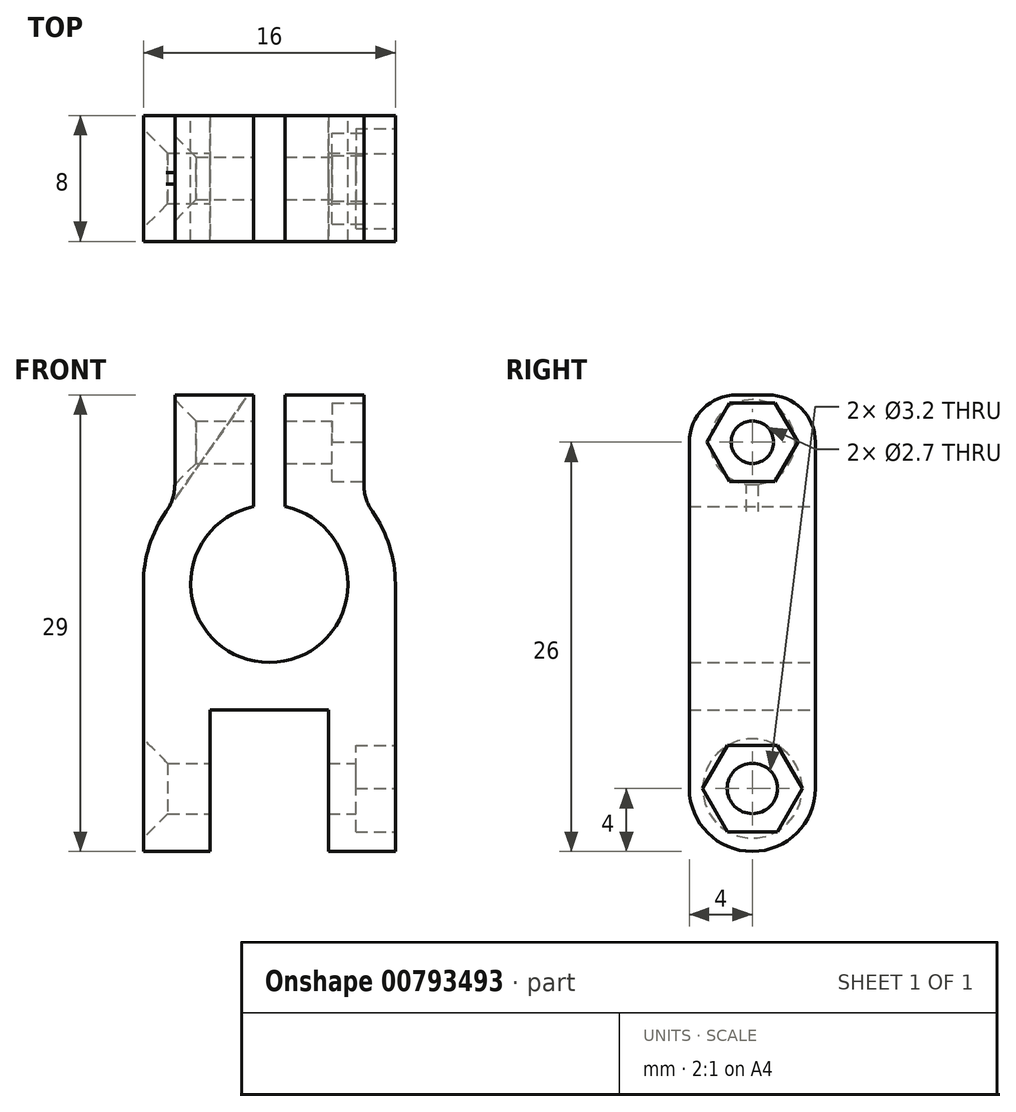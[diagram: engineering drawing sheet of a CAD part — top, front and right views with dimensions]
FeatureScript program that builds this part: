
annotation { "Feature Type Name" : "Feature", "Feature Type Description" : "" }
export const myFeature = defineFeature(function(context is Context, id is Id, definition is map)
    precondition{}
    {
        {
            var Q0;
            Q0=qCreatedBy(makeId("Front.planeOp"),FACE);
            var sketch = newSketch(context, id + "F0", { "sketchPlane" : qUnion([Q0])});
            skArc(sketch, "E0", {"start": v(-1, 4.9) * mm, "mid": v(0, -5) * mm, "end": v(1, 4.9) * mm});
            skLineSegment(sketch, "E1", {"start": v(-1, 12) * mm, "end": v(-1, 4.9) * mm});
            skLineSegment(sketch, "E2", {"start": v(1, 4.9) * mm, "end": v(1, 12) * mm});
            skLineSegment(sketch, "E3", {"start": v(6, 12) * mm, "end": v(1, 12) * mm});
            skLineSegment(sketch, "E4", {"start": v(-8, -17) * mm, "end": v(-3.75, -17) * mm});
            skLineSegment(sketch, "E5", {"start": v(-3.75, -17) * mm, "end": v(-3.75, -8) * mm});
            skLineSegment(sketch, "E6.MirrorCS", {"start": v(3.75, -17) * mm, "end": v(3.75, -8) * mm});
            skLineSegment(sketch, "E7.MirrorCS", {"start": v(8, -17) * mm, "end": v(3.75, -17) * mm});
            skLineSegment(sketch, "E8", {"start": v(-3.75, -8) * mm, "end": v(3.75, -8) * mm});
            skLineSegment(sketch, "E9", {"start": v(6, 12) * mm, "end": v(6, 5.3) * mm});
            skArc(sketch, "E10", {"start": v(8, 0) * mm, "mid": v(7.48, 2.83) * mm, "end": v(6, 5.3) * mm});
            skArc(sketch, "E11.MirrorCS", {"start": v(-8, 0) * mm, "mid": v(-7.48, 2.83) * mm, "end": v(-6, 5.3) * mm});
            skLineSegment(sketch, "E12.MirrorCS", {"start": v(-6, 12) * mm, "end": v(-1, 12) * mm});
            skLineSegment(sketch, "E13.MirrorCS", {"start": v(-6, 12) * mm, "end": v(-6, 5.3) * mm});
            skLineSegment(sketch, "E14", {"start": v(-8, -17) * mm, "end": v(-8, 0) * mm});
            skLineSegment(sketch, "E15", {"start": v(8, 0) * mm, "end": v(8, -17) * mm});
            skSolve(sketch);
        }
        {
            var Q0;
            Q0=makeQuery(id+"F0.imprint","IMPRINT",FACE,{"disambiguationData":[TD([[makeQuery(id+"F0.imprint","IMPRINT",EDGE,{"derivedFrom":sQuery(id+"F0.wireOp",EDGE,"E0")}),-1.0]])]});
            var Q1;
            {var subQ0=sQuery(id+"F0.wireOp",EDGE,"gT4Yp9KQ-vHPQ-P8ZU-SFqX-VDEBA4EE69W3");Q1=makeQuery(id+"F0.imprint","IMPRINT",FACE,{"disambiguationData":[TD([[makeQuery(id+"F0.imprint","IMPRINT",EDGE,{"derivedFrom":subQ0}),1.0]])]});}
            extrude(context, id + "F1", {"entities" : qUnion([Q0, Q1]), "endBound" : BoundingType.SYMMETRIC, "depth" : 8 * mm, "offsetDistance" : 25 * mm});
        }
        {
            var Q0;
            Q0=makeQuery(id+"F1.opExtrude","SWEPT_FACE",FACE,{"disambiguationData":[OSD([sQuery(id+"F0.wireOp",EDGE,"E9")])]});
            var sketch = newSketch(context, id + "F2", { "sketchPlane" : qUnion([Q0])});
            skCircle(sketch, "E16", {"center": v(0, 9) * mm, "radius": 1.35 * mm});
            skCircle(sketch, "E17.cCircle", {"center": v(0, 9) * mm, "radius": 2.5 * mm, "construction": true});
            skLineSegment(sketch, "E17.0", {"start": v(1.44, 11.5) * mm, "end": v(2.89, 9) * mm});
            skLineSegment(sketch, "E17.1", {"start": v(2.89, 9) * mm, "end": v(1.44, 6.5) * mm});
            skLineSegment(sketch, "E17.2", {"start": v(1.44, 6.5) * mm, "end": v(-1.44, 6.5) * mm});
            skLineSegment(sketch, "E17.3", {"start": v(-1.44, 6.5) * mm, "end": v(-2.89, 9) * mm});
            skLineSegment(sketch, "E17.4", {"start": v(-2.89, 9) * mm, "end": v(-1.44, 11.5) * mm});
            skLineSegment(sketch, "E17.5", {"start": v(-1.44, 11.5) * mm, "end": v(1.44, 11.5) * mm});
            skPoint(sketch, "E17.0.midPoint", {"position": v(2.17, 10.25) * mm});
            skSolve(sketch);
        }
        {
            var Q0;
            Q0=makeQuery(id+"F2.imprint","IMPRINT",FACE,{"disambiguationData":[TD([[makeQuery(id+"F2.imprint","IMPRINT",EDGE,{"derivedFrom":sQuery(id+"F2.wireOp",EDGE,"E16")}),1.0]])]});
            extrude(context, id + "F3", {"entities" : qUnion([Q0]), "operationType" : NewBodyOperationType.REMOVE, "endBound" : BoundingType.THROUGH_ALL, "oppositeDirection" : true, "depth" : 25 * mm, "offsetDistance" : 25 * mm});
        }
        {
            var Q0;
            Q0=makeQuery(id+"F2.imprint","IMPRINT",FACE,{"disambiguationData":[TD([[makeQuery(id+"F2.imprint","IMPRINT",EDGE,{"derivedFrom":sQuery(id+"F2.wireOp",EDGE,"E16")}),-1.0]])]});
            extrude(context, id + "F4", {"entities" : qUnion([Q0]), "operationType" : NewBodyOperationType.REMOVE, "oppositeDirection" : true, "depth" : 2 * mm, "offsetDistance" : 25 * mm});
        }
        {
            var Q0;
            Q0=makeQuery(id+"F1.opExtrude","SWEPT_FACE",FACE,{"disambiguationData":[OSD([sQuery(id+"F0.wireOp",EDGE,"E15")])]});
            var sketch = newSketch(context, id + "F5", { "sketchPlane" : qUnion([Q0])});
            skCircle(sketch, "E18", {"center": v(0, -13) * mm, "radius": 1.6 * mm});
            skCircle(sketch, "E19.cCircle", {"center": v(0, -13) * mm, "radius": 2.75 * mm, "construction": true});
            skLineSegment(sketch, "E19.0", {"start": v(-1.59, -10.25) * mm, "end": v(1.59, -10.25) * mm});
            skLineSegment(sketch, "E19.1", {"start": v(1.59, -10.25) * mm, "end": v(3.18, -13) * mm});
            skLineSegment(sketch, "E19.2", {"start": v(3.18, -13) * mm, "end": v(1.59, -15.75) * mm});
            skLineSegment(sketch, "E19.3", {"start": v(1.59, -15.75) * mm, "end": v(-1.59, -15.75) * mm});
            skLineSegment(sketch, "E19.4", {"start": v(-1.59, -15.75) * mm, "end": v(-3.18, -13) * mm});
            skLineSegment(sketch, "E19.5", {"start": v(-3.18, -13) * mm, "end": v(-1.59, -10.25) * mm});
            skPoint(sketch, "E19.0.midPoint", {"position": v(0, -10.25) * mm});
            skSolve(sketch);
        }
        {
            var Q0;
            Q0=makeQuery(id+"F5.imprint","IMPRINT",FACE,{"disambiguationData":[TD([[makeQuery(id+"F5.imprint","IMPRINT",EDGE,{"derivedFrom":sQuery(id+"F5.wireOp",EDGE,"E18")}),1.0]])]});
            var Q1;
            {var subQ0=sQuery(id+"F5.wireOp",EDGE,"dgfmRsRT-HZR4-KMtm-UVD4-OGYZ9sb2hiea");var subQ1=sQuery(id+"F0.wireOp",EDGE,"URoOaodK-mer2-KlBf-KcxF-PiR6j1BPeDQ6");var subQ2=makeQuery(id+"F1.opExtrude","CAP_EDGE",EDGE,{"disambiguationData":[OSD([subQ1])],"isStart":false});var subQ3=makeQuery(id+"F5.imprint","INTERSECT",VERTEX,{"derivedFrom":[subQ2,sQuery(id+"F5.wireOp",EDGE,"iwAXt04E-8AKp-sdOK-APD1-idUJ9iq6WJ0X"),subQ0]});Q1=makeQuery(id+"F5.imprint","IMPRINT",FACE,{"disambiguationData":[TD([[makeQuery(id+"F5.imprint","IMPRINT",EDGE,{"disambiguationData":[TD([[subQ3,-1.0]])],"derivedFrom":subQ0}),-1.0]])]});}
            var Q2;
            {var subQ0=sQuery(id+"F5.wireOp",EDGE,"dgfmRsRT-HZR4-KMtm-UVD4-OGYZ9sb2hiea");var subQ1=sQuery(id+"F0.wireOp",EDGE,"URoOaodK-mer2-KlBf-KcxF-PiR6j1BPeDQ6");var subQ2=makeQuery(id+"F1.opExtrude","CAP_EDGE",EDGE,{"disambiguationData":[OSD([subQ1])],"isStart":true});var subQ3=makeQuery(id+"F5.imprint","INTERSECT",VERTEX,{"derivedFrom":[subQ2,sQuery(id+"F5.wireOp",EDGE,"2524a595-133a-427d-9363-88fda697d8180.MirrorCS"),subQ0]});Q2=makeQuery(id+"F5.imprint","IMPRINT",FACE,{"disambiguationData":[TD([[makeQuery(id+"F5.imprint","IMPRINT",EDGE,{"disambiguationData":[TD([[subQ3,1.0]])],"derivedFrom":subQ0}),-1.0]])]});}
            extrude(context, id + "F6", {"entities" : qUnion([Q0, Q1, Q2]), "operationType" : NewBodyOperationType.REMOVE, "oppositeDirection" : true, "depth" : 25 * mm, "offsetDistance" : 25 * mm});
        }
        {
            var Q0;
            Q0=makeQuery(id+"F5.imprint","IMPRINT",FACE,{"disambiguationData":[TD([[makeQuery(id+"F5.imprint","IMPRINT",EDGE,{"derivedFrom":sQuery(id+"F5.wireOp",EDGE,"E18")}),-1.0]])]});
            var Q1;
            Q1 = qSketchRegion(id + "FS4RhZu42dw0kxH_1", true);
            extrude(context, id + "F7", {"entities" : qUnion([Q0, Q1]), "operationType" : NewBodyOperationType.REMOVE, "oppositeDirection" : true, "depth" : 2.5 * mm, "offsetDistance" : 25 * mm});
        }
        {
            var Q0;
            Q0=makeQuery(id+"F3.boolean.opBoolean","INTERSECT",EDGE,{"derivedFrom":[makeQuery(id+"F1.opExtrude","SWEPT_FACE",FACE,{"disambiguationData":[OSD([sQuery(id+"F0.wireOp",EDGE,"E13.MirrorCS")])]}),makeQuery(id+"F3.opExtrude","SWEPT_FACE",FACE,{"disambiguationData":[OSD([sQuery(id+"F2.wireOp",EDGE,"E16")])]})]});
            chamfer(context, id + "F8", {"entities" : qUnion([Q0]), "width" : 1.35 * mm, "tangentPropagation" : true});
        }
        {
            var Q0;
            Q0=makeQuery(id+"F1.opExtrude","CAP_EDGE",EDGE,{"disambiguationData":[OSD([sQuery(id+"F0.wireOp",EDGE,"E12.MirrorCS")])],"isStart":false});
            var Q1;
            Q1=makeQuery(id+"F1.opExtrude","CAP_EDGE",EDGE,{"disambiguationData":[OSD([sQuery(id+"F0.wireOp",EDGE,"E3")])],"isStart":false});
            var Q2;
            Q2=makeQuery(id+"F1.opExtrude","CAP_EDGE",EDGE,{"disambiguationData":[OSD([sQuery(id+"F0.wireOp",EDGE,"E3")])],"isStart":true});
            var Q3;
            Q3=makeQuery(id+"F1.opExtrude","CAP_EDGE",EDGE,{"disambiguationData":[OSD([sQuery(id+"F0.wireOp",EDGE,"E12.MirrorCS")])],"isStart":true});
            var Q4;
            Q4=makeQuery(id+"F1.opExtrude","SWEPT_EDGE",EDGE,{"disambiguationData":[OSD([sQuery(id+"F0.wireOp",EDGE,"E9"),sQuery(id+"F0.wireOp",EDGE,"E10")])]});
            var Q5;
            Q5=makeQuery(id+"F1.opExtrude","SWEPT_EDGE",EDGE,{"disambiguationData":[OSD([sQuery(id+"F0.wireOp",EDGE,"E11.MirrorCS"),sQuery(id+"F0.wireOp",EDGE,"E13.MirrorCS")])]});
            fillet(context, id + "F9", {"entities" : qUnion([Q0, Q1, Q2, Q3, Q4, Q5]), "radius" : 3 * mm, "tangentPropagation" : true, "allowEdgeOverflow" : false});
        }
        {
            var Q0;
            Q0=makeQuery(id+"F1.opExtrude","CAP_EDGE",EDGE,{"disambiguationData":[OSD([sQuery(id+"F0.wireOp",EDGE,"E7.MirrorCS")])],"isStart":false});
            var Q1;
            Q1=makeQuery(id+"F1.opExtrude","CAP_EDGE",EDGE,{"disambiguationData":[OSD([sQuery(id+"F0.wireOp",EDGE,"E4")])],"isStart":false});
            var Q2;
            Q2=makeQuery(id+"F1.opExtrude","CAP_EDGE",EDGE,{"disambiguationData":[OSD([sQuery(id+"F0.wireOp",EDGE,"E4")])],"isStart":true});
            var Q3;
            Q3=makeQuery(id+"F1.opExtrude","CAP_EDGE",EDGE,{"disambiguationData":[OSD([sQuery(id+"F0.wireOp",EDGE,"E7.MirrorCS")])],"isStart":true});
            fillet(context, id + "F10", {"entities" : qUnion([Q0, Q1, Q2, Q3]), "radius" : 4 * mm, "tangentPropagation" : true, "allowEdgeOverflow" : false});
        }
        {
            var Q0;
            Q0=makeQuery(id+"F6.boolean.opBoolean","INTERSECT",EDGE,{"derivedFrom":[makeQuery(id+"F1.opExtrude","SWEPT_FACE",FACE,{"disambiguationData":[OSD([sQuery(id+"F0.wireOp",EDGE,"E14")])]}),makeQuery(id+"F6.opExtrude","SWEPT_FACE",FACE,{"disambiguationData":[OSD([sQuery(id+"F5.wireOp",EDGE,"E18")])]})]});
            chamfer(context, id + "F11", {"entities" : qUnion([Q0]), "width" : 1.55 * mm, "tangentPropagation" : true});
        }
    });
